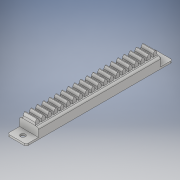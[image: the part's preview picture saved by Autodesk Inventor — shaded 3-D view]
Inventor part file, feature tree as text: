
AUTODESK INVENTOR PART (.ipt)
format: ipt  version: 2018 (Build 220112000, 112)  size: 376,320 bytes
history: native  units: in
note: dims shown in document units (in); Inventor stores cm internally (conversion verified against a paired STEP export)
features: extrude x6, sketch x6, projected_geometry x2, fillet x1
ambient origin geometry x8: Origin, YZ Plane, XZ Plane, XY Plane, X Axis, Y Axis, Z Axis, Center Point
bodies: Body1 (feature_tree)
feature tree (15):
  extrude  "Extrusion2"  Depth=2.5in
  sketch  "Sketch3"  dims[d6=0.385in d7=0.0in d9=0.092in]
  extrude  "Extrusion8"  Depth=0.385in
  extrude  "Extrusion12"  Depth=0.5814in
  extrude  "Extrusion13"  Depth=0.25in TaperAngle=0.0deg
  extrude  "Extrusion14"  Depth=2.5in
  extrude  "Extrusion15"  Depth=0.25in
  fillet  "Fillet1"  Radius=0.25in
  sketch  "Sketch2"  dims[d4=2.5in d5=0.435in]
  sketch  "Sketch10"  dims[d63=0.5814in d64=0.5814in]
  sketch  "Sketch11"  dims[d72=7.874in d74=0.1271in d75=0.3937in d77=1.0in d79=0.25in d80=0.0in]
  projected_geometry  "Projected Loop5"
  sketch  "Sketch12"  dims[d91=1.0in d92=0.0in d93=2.5in]
  projected_geometry  "Projected Loop6"
  sketch  "Sketch13"  dims[d95=0.1378in d96=0.0in d97=0.25in d98=0.25in d99=0.0394in d100=0.0in d101=0.0984in d102=0.0984in d103=0.0394in d104=0.0in d105=0.0394in]
